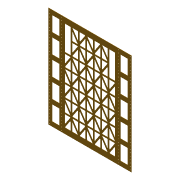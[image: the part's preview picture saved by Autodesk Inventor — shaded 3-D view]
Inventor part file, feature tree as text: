
AUTODESK INVENTOR PART (.ipt)
format: ipt  version: 2015 (Build 190159000, 159)  size: 1,620,480 bytes
history: native  units: in
note: dims shown in document units (in); Inventor stores cm internally (conversion verified against a paired STEP export)
features: sketch x4, other x2, extrude x1, hole x1, fillet x1
ambient origin geometry x8: Origin, YZ Plane, XZ Plane, XY Plane, X Axis, Y Axis, Z Axis, Center Point
bodies: Solid1 (feature_tree)
feature tree (9):
  extrude  "Extrusion1"  Depth=34.0in
  hole  "Hole1"  [1 undecoded]
  fillet  "Fillet1"  Radius=2.0in
  sketch  "Sketch1"  dims[d0=28.0in d1=34.0in]
  sketch  "Sketch2"  dims[d2=2.0in d3=3.0in d4=2.0in]
  sketch  "Sketch3"  dims[d5=3.0in]
  sketch  "Sketch4"  dims[d6=0.901in d7=5.5in d8=1.8465in d9=0.25in d10=0.125in d11=0.25in d12=1.1811in d14=5.0in d15=1.1811in d17=8.802in d20=0.25in d22=3.0in d23=2.0in d24=0.901in d25=2.0in d26=0.5in d27=0.125in d28=1.1811in d30=5.0in d31=0.3937in d33=1.0in d35=0.09in d36=0.0in d37=0.5in d38=4.5in d39=4.5in d40=0.5in d41=0.5in d42=13.3858in d44=1.0in d45=0.3937in d47=1.0in d49=0.266in d50=0.75in d51=0.375in d52=0.25in d53=0.5635in d54=0.12in d55=0.8108in d56=1.25in d57=1.5in d58=3.75in d59=5.0in d60=0.125in d61=1.9685in d63=6.5in d64=0.7874in d66=23.0in d69=0.12in d70=0.0in d71=0.0in d72=0.0in d73=0.0in d74=0.0in d75=0.125in d76=14.0in d77=0.0in d78=0.0in d79=0.0in d80=0.125in d81=0.12in d82=0.0in d83=0.125in]
  other  "Cut1"
  other  "Cut2"
note: 1 required parameter value undecoded (feature->parameter linkage not recoverable at this tier; creation-order binding heuristic only, values carry confidence <= 0.55)
